# Revit family: Fluxor WC Public
name_source: partatom
category: Plumbing Fixtures
revit_build: Autodesk Revit 2015 (Build: 20140322_1515(x64)
units: mm (PartAtom-declared; Revit-internal decimal feet)

## types (1)
- Fluxor WC Public
    Assembly Code = D2010.60
    BT_Color = Cromo
    BT_Itemizado_Estandar_CDT = E 04 02 00
    BT_Material = Latón Cromado
    BT_SKU = 00 00 00
    BT_Uso = Fluxómetro
    Default Elevation = 1219 mm
    Depth = 272 mm
    Description = Fluxor expuesto para wc
    Height = 326 mm
    ID_Objeto = BT_F_F_1813
    ID_Source = BIMTOOL
    Keynote = 22 41 13.13
    Manufacturer = Klipen
    Model = Fluxor WC Public
    Supplier = Mk
    Type Comments = Fluxor expuesto para wc
Litros de descarga: 4,8 
Conexión a muro: 1” HI 
Tiempo: 4-8 segundos
Presión de trabajo: 2 - 4 BAR 
Terminación: Cromo
    URL = www.mk.cl
    Width = 80 mm

## geometry (parser evidence)
native form markers: Blend x6, Extrusion x2, Sweep x4
no freeform markers — native parametric forms only
